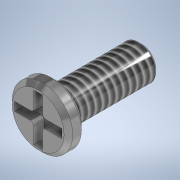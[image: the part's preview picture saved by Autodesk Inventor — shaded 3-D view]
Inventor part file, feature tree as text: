
AUTODESK INVENTOR PART (.ipt)
format: ipt  version: 2021 (Build 250183000, 183)  size: 157,184 bytes
history: native  units: mm
features: extrude x3, sketch x3, chamfer x2, other x1, thread x1, fillet x1
ambient origin geometry x8: Origin, YZ Plane, XZ Plane, XY Plane, X Axis, Y Axis, Z Axis, Center Point
bodies: Body1 (feature_tree)
feature tree (11):
  other  "Sólido1"
  extrude  "Extrusão1"  Depth=5.0mm TaperAngle=0.0deg
  extrude  "Extrusão2"  Depth=1.0mm TaperAngle=0.0deg
  extrude  "Extrusão3"  Depth=0.5mm
  thread  "Rosca1"  [1 undecoded]
  fillet  "Arredondamento2"  Radius=2.75mm
  chamfer  "Chanfro1"  Distance=0.6mm
  chamfer  "Chanfro2"  Distance=15.255mm
  sketch  "Esboço1"  dims[d0=2.0mm d1=5.0mm d2=0.0mm]
  sketch  "Esboço2"  dims[d3=3.5mm d4=1.0mm d5=0.0mm]
  sketch  "Esboço3"  dims[d6=0.5mm d7=0.5mm d8=2.75mm d9=2.75mm d10=0.6mm d11=0.0mm d13=15.255mm d14=0.0mm d15=0.2mm d16=0.25mm d17=2.0mm d18=45.0deg d19=0.2mm d20=2.0mm d21=45.0deg]
note: 1 required parameter value undecoded (feature->parameter linkage not recoverable at this tier; creation-order binding heuristic only, values carry confidence <= 0.55)
